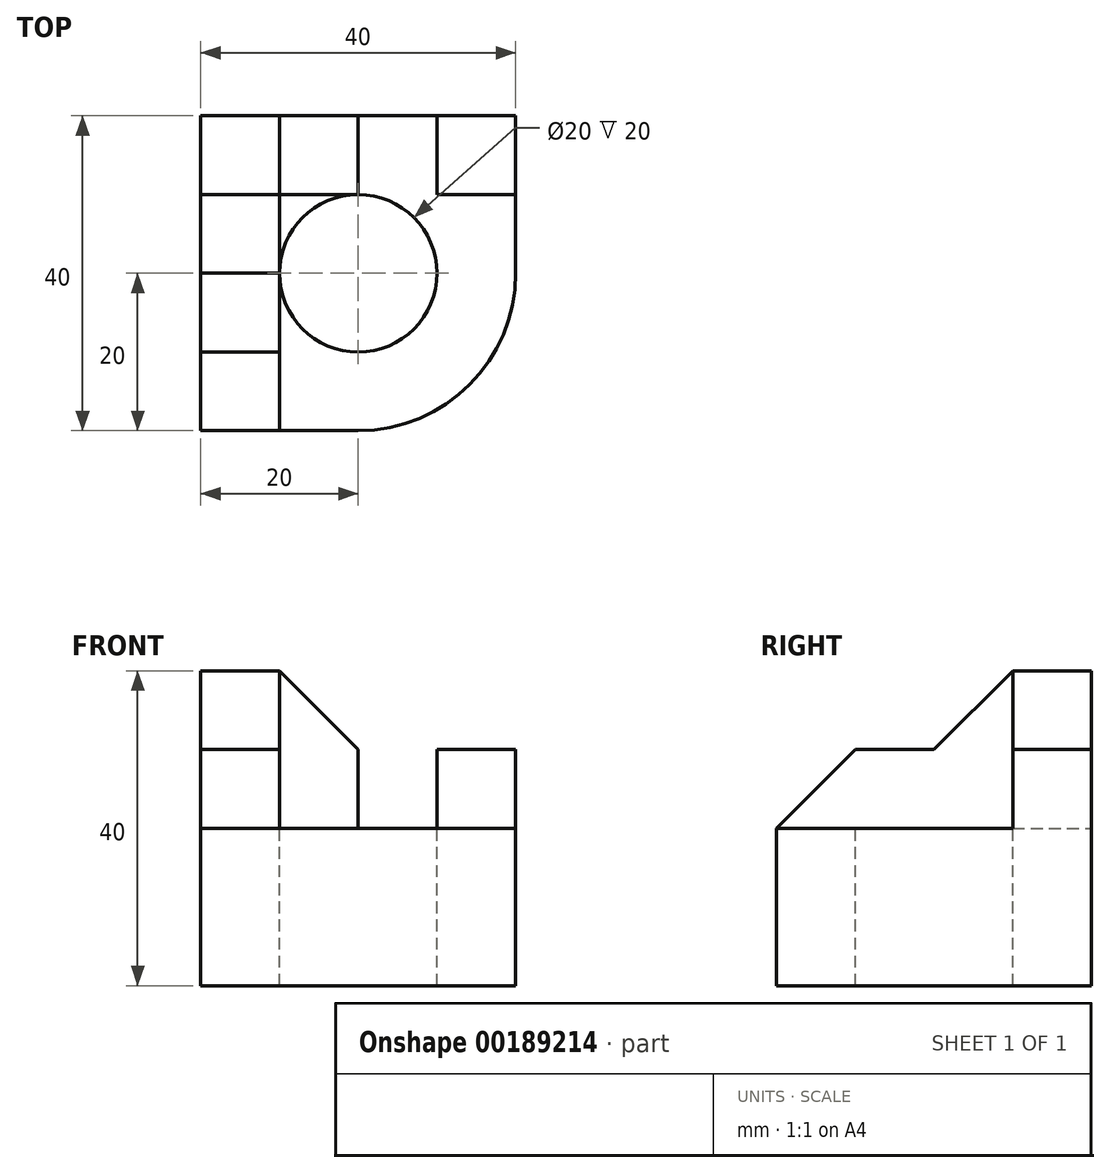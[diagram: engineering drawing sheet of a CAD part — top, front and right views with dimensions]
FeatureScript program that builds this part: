
annotation { "Feature Type Name" : "Feature", "Feature Type Description" : "" }
export const myFeature = defineFeature(function(context is Context, id is Id, definition is map)
    precondition{}
    {
        {
            var Q0;
            Q0=qCreatedBy(makeId("Top.planeOp"),FACE);
            var sketch = newSketch(context, id + "F0", { "sketchPlane" : qUnion([Q0])});
            skLineSegment(sketch, "E0.bottom", {"start": v(0, 0) * mm, "end": v(20, 0) * mm});
            skLineSegment(sketch, "E0.top", {"start": v(0, 40) * mm, "end": v(40, 40) * mm});
            skLineSegment(sketch, "E0.left", {"start": v(0, 0) * mm, "end": v(0, 40) * mm});
            skLineSegment(sketch, "E0.right", {"start": v(40, 20) * mm, "end": v(40, 40) * mm});
            skPoint(sketch, "E1.visualSharp", {"position": v(40, 0) * mm});
            skArc(sketch, "E1.filletArc", {"start": v(20, 0) * mm, "mid": v(34.14, 5.86) * mm, "end": v(40, 20) * mm});
            skSolve(sketch);
        }
        {
            var Q0;
            Q0=makeQuery(id+"F0.imprint","IMPRINT",FACE,{"disambiguationData":[TD([[makeQuery(id+"F0.imprint","IMPRINT",EDGE,{"derivedFrom":sQuery(id+"F0.wireOp",EDGE,"E0.bottom")}),1.0]])]});
            extrude(context, id + "F1", {"entities" : qUnion([Q0]), "depth" : 20 * mm});
        }
        {
            var Q0;
            Q0=makeQuery(id+"F1.opExtrude","CAP_FACE",FACE,{"disambiguationData":[OSD([sQuery(id+"F0.wireOp",EDGE,"E0.bottom"),sQuery(id+"F0.wireOp",EDGE,"E0.top"),sQuery(id+"F0.wireOp",EDGE,"E0.left"),sQuery(id+"F0.wireOp",EDGE,"E0.right"),sQuery(id+"F0.wireOp",EDGE,"E1.filletArc")])],"isStart":false});
            var sketch = newSketch(context, id + "F2", { "sketchPlane" : qUnion([Q0])});
            skCircle(sketch, "E2", {"center": v(20, 20) * mm, "radius": 10 * mm});
            skSolve(sketch);
        }
        {
            var Q0;
            Q0=makeQuery(id+"F2.imprint","IMPRINT",FACE,{"disambiguationData":[TD([[makeQuery(id+"F2.imprint","IMPRINT",EDGE,{"derivedFrom":sQuery(id+"F2.wireOp",EDGE,"E2")}),1.0]])]});
            extrude(context, id + "F3", {"entities" : qUnion([Q0]), "operationType" : NewBodyOperationType.REMOVE, "endBound" : BoundingType.THROUGH_ALL, "oppositeDirection" : true, "depth" : 25 * mm});
        }
        {
            var Q0;
            Q0=qCreatedBy(makeId("Right.planeOp"),FACE);
            var sketch = newSketch(context, id + "F4", { "sketchPlane" : qUnion([Q0])});
            skLineSegment(sketch, "E3", {"start": v(40, 20) * mm, "end": v(40, 40) * mm});
            skLineSegment(sketch, "E4", {"start": v(40, 40) * mm, "end": v(30, 40) * mm});
            skLineSegment(sketch, "E5", {"start": v(30, 40) * mm, "end": v(20, 30) * mm});
            skLineSegment(sketch, "E6", {"start": v(20, 30) * mm, "end": v(10, 30) * mm});
            skLineSegment(sketch, "E7", {"start": v(10, 30) * mm, "end": v(0, 20) * mm});
            skLineSegment(sketch, "E8.0", {"start": v(0, 20) * mm, "end": v(40, 20) * mm});
            skSolve(sketch);
        }
        {
            var Q0;
            Q0=makeQuery(id+"F4.imprint","IMPRINT",FACE,{"disambiguationData":[TD([[makeQuery(id+"F4.imprint","IMPRINT",EDGE,{"derivedFrom":sQuery(id+"F4.wireOp",EDGE,"E3")}),1.0]])]});
            extrude(context, id + "F5", {"entities" : qUnion([Q0]), "operationType" : NewBodyOperationType.ADD, "depth" : 10 * mm});
        }
        {
            var Q0;
            Q0=makeQuery(id+"F5.boolean.opBoolean","MERGE",FACE,{"derivedFrom":[makeQuery(id+"F1.opExtrude","SWEPT_FACE",FACE,{"disambiguationData":[OSD([sQuery(id+"F0.wireOp",EDGE,"E0.top")])]}),makeQuery(id+"F5.opExtrude","SWEPT_FACE",FACE,{"disambiguationData":[OSD([sQuery(id+"F4.wireOp",EDGE,"E3")])]})]});
            var sketch = newSketch(context, id + "F6", { "sketchPlane" : qUnion([Q0])});
            skLineSegment(sketch, "E9", {"start": v(-40, 20) * mm, "end": v(-40, 30) * mm});
            skLineSegment(sketch, "E10", {"start": v(-40, 30) * mm, "end": v(-30, 30) * mm});
            skLineSegment(sketch, "E11", {"start": v(-30, 30) * mm, "end": v(-30, 20) * mm});
            skLineSegment(sketch, "E12", {"start": v(-10, 40) * mm, "end": v(-20, 30) * mm});
            skLineSegment(sketch, "E13", {"start": v(-20, 30) * mm, "end": v(-20, 20) * mm});
            skLineSegment(sketch, "E14.0", {"start": v(-10, 20) * mm, "end": v(-20, 20) * mm});
            skLineSegment(sketch, "E15.trimOffspring", {"start": v(-30, 20) * mm, "end": v(-40, 20) * mm});
            skSolve(sketch);
        }
        {
            var Q0;
            Q0=makeQuery(id+"F6.imprint","IMPRINT",FACE,{"disambiguationData":[TD([[makeQuery(id+"F6.imprint","IMPRINT",EDGE,{"derivedFrom":sQuery(id+"F6.wireOp",EDGE,"E9")}),-1.0]])]});
            var Q1;
            Q1=makeQuery(id+"F6.imprint","IMPRINT",FACE,{"disambiguationData":[TD([[makeQuery(id+"F6.imprint","IMPRINT",EDGE,{"derivedFrom":sQuery(id+"F6.wireOp",EDGE,"E12")}),1.0]])]});
            extrude(context, id + "F7", {"entities" : qUnion([Q0, Q1]), "operationType" : NewBodyOperationType.ADD, "oppositeDirection" : true, "depth" : 10 * mm});
        }
    });
